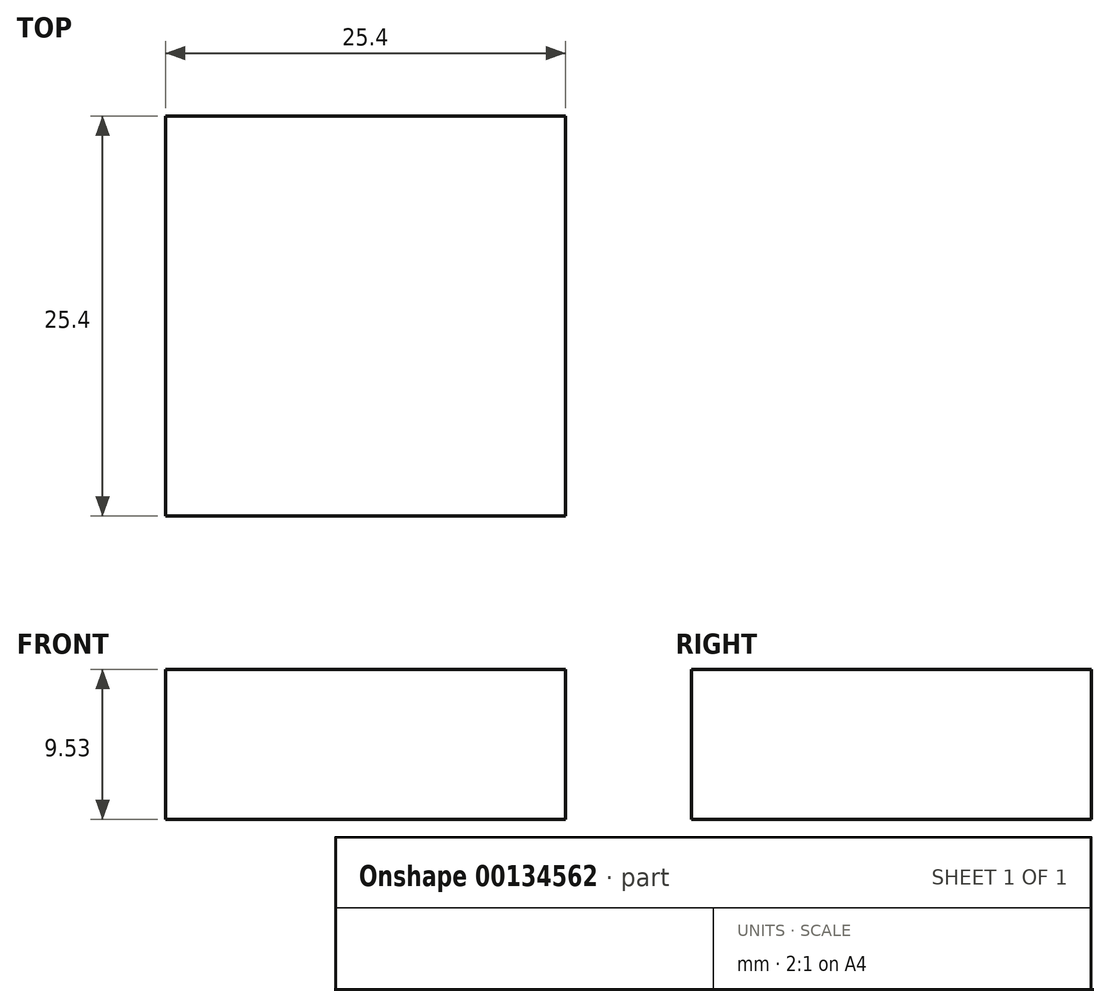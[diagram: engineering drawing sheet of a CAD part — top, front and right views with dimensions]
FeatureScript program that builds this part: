
annotation { "Feature Type Name" : "Feature", "Feature Type Description" : "" }
export const myFeature = defineFeature(function(context is Context, id is Id, definition is map)
    precondition{}
    {
        {
            var Q0;
            Q0=qCreatedBy(makeId("Top.planeOp"),FACE);
            var sketch = newSketch(context, id + "F0", { "sketchPlane" : qUnion([Q0])});
            skLineSegment(sketch, "E0.bottom", {"start": v(12.7, 12.7) * mm, "end": v(-12.7, 12.7) * mm});
            skLineSegment(sketch, "E0.top", {"start": v(12.7, -12.7) * mm, "end": v(-12.7, -12.7) * mm});
            skLineSegment(sketch, "E0.left", {"start": v(12.7, 12.7) * mm, "end": v(12.7, -12.7) * mm});
            skLineSegment(sketch, "E0.right", {"start": v(-12.7, 12.7) * mm, "end": v(-12.7, -12.7) * mm});
            skPoint(sketch, "E0.middle", {"position": v(0, 0) * mm});
            skSolve(sketch);
        }
        {
            var Q0;
            Q0 = qSketchRegion(id + "F0", true);
            extrude(context, id + "F1", {"entities" : qUnion([Q0]), "depth" : 9.52 * mm});
        }
    });
